# Revit family: Reece_Shower_GROHE_Rainshower_Single Shower_Smart Active_Square
name_source: partatom
category: Plumbing Fixtures
revit_build: Autodesk Revit 2018 (Build: 20180329_1100(x64)
units: mm (PartAtom-declared; Revit-internal decimal feet)

## family parameters
Always vertical = Yes
Cut with Voids When Loaded = Yes
Part Type = Normal
Room Calculation Point = Yes
Round Connector Dimension = Use Diameter
Shared = Yes
Work Plane-Based = Yes

## types (1)
- Chrome
    Default Elevation = 0 mm  [stored 0 ft]
    Description = GROHE Rainshower SmartActive Single Rail Shower Square Chrome (4 Star)
    Disclaimer = THIS FILE IS THE PROPERTY OF THE REECE GROUP. IT MAY NOT BE REPRODUCED, REVERSE-ENGINEERED OR MODIFIED. ANY REPUBLICATION, TRANSMISSION OR DISTRIBUTION FOR THE PURPOSE OF COMMERCIALLY EXPLOITING THE FILES IS PROHIBITED.
    Keynote = Product #9508997, Reece_Shower_GROHE_Rainshower_Single Shower_Smart Active_Square - Chrome
    Manufacturer = GROHE
    Model = SmartActive
    Reece_Detail_Additional = Single Rail Shower
    Reece_Detail_Disclaimer = THIS FILE IS THE PROPERTY OF THE REECE GROUP. IT MAY NOT BE REPRODUCED, REVERSE-ENGINEERED OR MODIFIED. ANY REPUBLICATION, TRANSMISSION OR DISTRIBUTION FOR THE PURPOSE OF COMMERCIALLY EXPLOITING THE FILES IS PROHIBITED.
    Reece_Detail_Shape = Square
    Reece_Material_Colour = Reece_Safety Glass_Opaque
    Reece_Material_Main = Reece_Brass_Chrome
    Reece_Material_Secondary = Reece_Plastic_White
    Reece_Overall_Height = 752 mm  [stored 2.46719 ft]
    Reece_Overall_Length = 630 mm  [stored 2.06693 ft]
    Reece_Overall_Width = 140 mm  [stored 0.459318 ft]
    Reece_Product_Brand = GROHE
    Reece_Product_Description = GROHE Rainshower SmartActive Single Rail Shower Square with Wall Water Inlet Chrome (3 Star)
    Reece_Product_Mount = Wall Mounted
    Reece_Product_Number = 9508997
    Reece_Product_Sub Brand = SmartActive
    Reece_Product_Type = Shower
    Reece_Product_Web Page = https://www.reece.com.au
    Reece_Shower_Inlet = 12 mm  [stored 0.0393701 ft]
    Type Comments = Shower
    URL = https://www.reece.com.au

note: [stored X ft] marks values corroborated as IEEE doubles in the binary element streams (Revit-internal decimal feet)

## geometry (parser evidence)
native form markers: Sweep x16
no freeform markers — native parametric forms only
